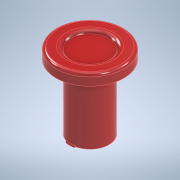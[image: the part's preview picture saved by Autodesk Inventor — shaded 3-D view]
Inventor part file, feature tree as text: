
AUTODESK INVENTOR PART (.ipt)
format: ipt  version: 2022 (Build 260153000, 153)  size: 166,912 bytes
history: native  units: mm
features: sketch x3, extrude x2, fillet x2, revolve x1
ambient origin geometry x8: Origin, YZ Plane, XZ Plane, XY Plane, X Axis, Y Axis, Z Axis, Center Point
bodies: Solid1 (feature_tree)
feature tree (8):
  revolve  "Revolution1"  [1 undecoded]
  extrude  "Extrusion1"  Depth=1.0mm
  fillet  "Fillet1"  Radius=14.0mm
  fillet  "Fillet2"  [1 undecoded]
  extrude  "Extrusion2"  Depth=1.0mm TaperAngle=0.0deg
  sketch  "Sketch2"  dims[d0=4.0mm d2=25.0mm]
  sketch  "Sketch3"  dims[d3=28.0mm d4=1.0mm d5=14.0mm d6=90.0deg]
  sketch  "Sketch4"  dims[d7=14.0mm d8=1.0mm d9=0.0mm d10=2.0mm d11=1.0mm d12=0.5mm d13=1.584493mm d14=1.584493mm d15=1.584493mm d16=1.584493mm d17=0.5mm d18=0.0mm]
note: 2 required parameter values undecoded (feature->parameter linkage not recoverable at this tier; creation-order binding heuristic only, values carry confidence <= 0.55)